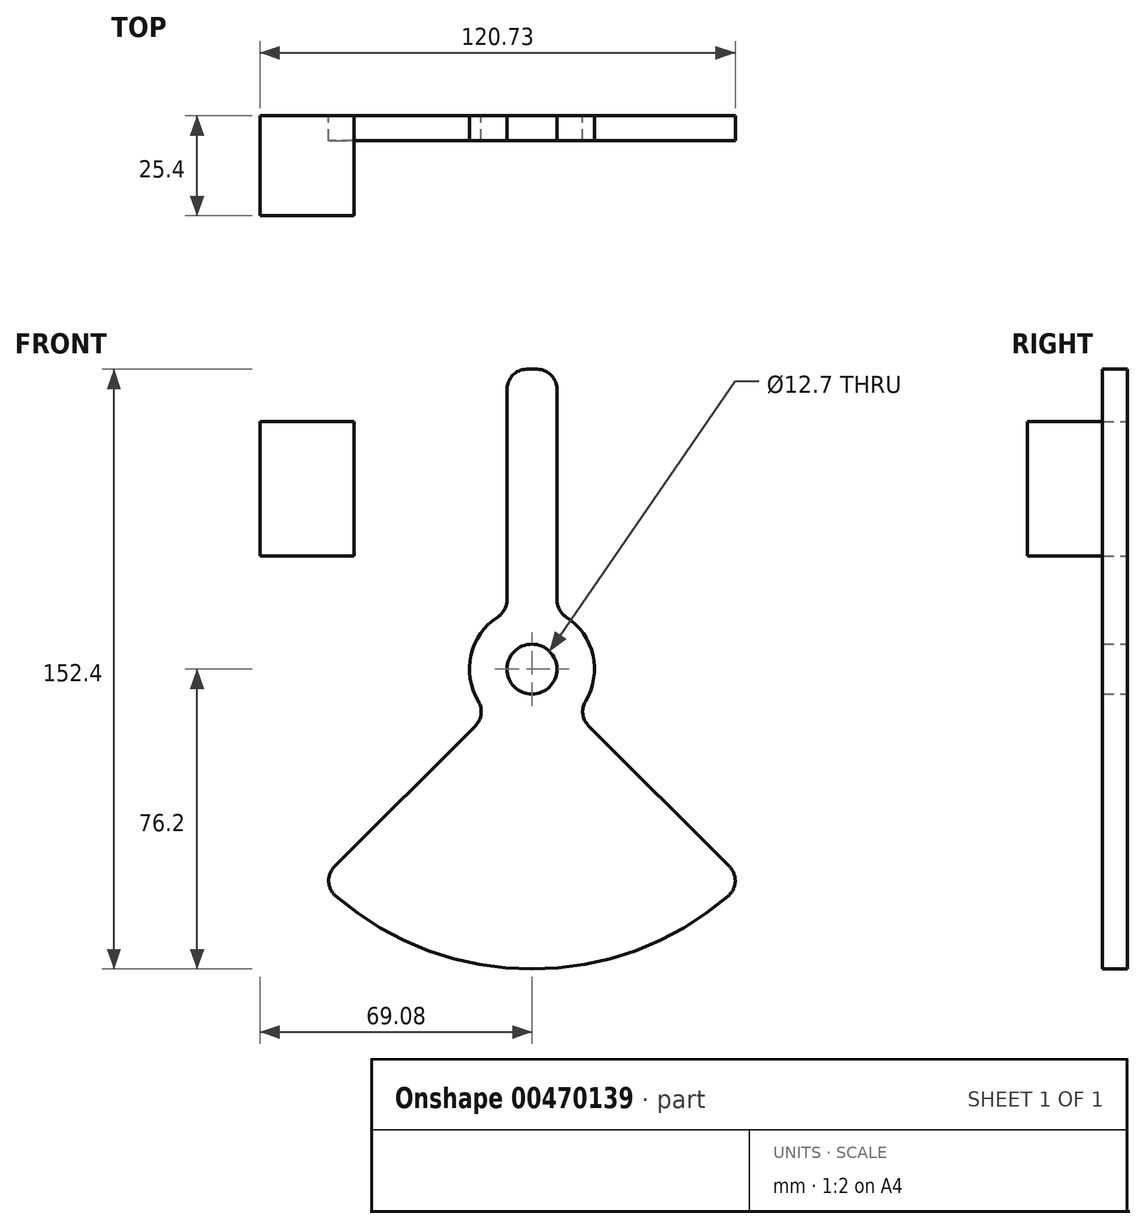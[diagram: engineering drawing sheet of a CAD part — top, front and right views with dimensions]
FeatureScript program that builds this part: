
annotation { "Feature Type Name" : "Feature", "Feature Type Description" : "" }
export const myFeature = defineFeature(function(context is Context, id is Id, definition is map)
    precondition{}
    {
        {
            var Q0;
            Q0=qCreatedBy(makeId("Front.planeOp"),FACE);
            var sketch = newSketch(context, id + "F0", { "sketchPlane" : qUnion([Q0])});
            skCircle(sketch, "E0", {"center": v(0, 0) * mm, "radius": 15.88 * mm});
            skCircle(sketch, "E1", {"center": v(0, 0) * mm, "radius": 76.2 * mm});
            skCircle(sketch, "E2", {"center": v(0, 0) * mm, "radius": 66.67 * mm});
            skCircle(sketch, "E3", {"center": v(0, 0) * mm, "radius": 6.35 * mm});
            skLineSegment(sketch, "E4", {"start": v(-6.35, 14.55) * mm, "end": v(-6.35, 75.93) * mm});
            skLineSegment(sketch, "E5", {"start": v(-6.35, 75.93) * mm, "end": v(6.35, 75.93) * mm, "construction": true});
            skLineSegment(sketch, "E6", {"start": v(6.35, 75.93) * mm, "end": v(6.35, 14.55) * mm});
            skPoint(sketch, "E7", {"position": v(0, 75.93) * mm});
            skLineSegment(sketch, "E8", {"start": v(-11.23, -11.23) * mm, "end": v(-53.88, -53.88) * mm});
            skLineSegment(sketch, "E9", {"start": v(53.88, -53.88) * mm, "end": v(11.23, -11.23) * mm});
            skSolve(sketch);
        }
        {
            var Q0;
            {var subQ0=sQuery(id+"F0.wireOp",EDGE,"E4");var subQ1=sQuery(id+"F0.wireOp",EDGE,"E0");var subQ2=makeQuery(id+"F0.imprint","INTERSECT",VERTEX,{"derivedFrom":[subQ1,subQ0]});Q0=makeQuery(id+"F0.imprint","IMPRINT",FACE,{"disambiguationData":[TD([[makeQuery(id+"F0.imprint","IMPRINT",EDGE,{"disambiguationData":[TD([[subQ2,1.0]])],"derivedFrom":subQ1}),-1.0]])]});}
            var Q1;
            {var subQ0=sQuery(id+"F0.wireOp",EDGE,"E4");var subQ1=sQuery(id+"F0.wireOp",EDGE,"E1");var subQ2=makeQuery(id+"F0.imprint","INTERSECT",VERTEX,{"derivedFrom":[subQ1,subQ0]});Q1=makeQuery(id+"F0.imprint","IMPRINT",FACE,{"disambiguationData":[TD([[makeQuery(id+"F0.imprint","IMPRINT",EDGE,{"disambiguationData":[TD([[subQ2,1.0]])],"derivedFrom":subQ1}),1.0]])]});}
            var Q2;
            Q2=makeQuery(id+"F0.imprint","IMPRINT",FACE,{"disambiguationData":[TD([[makeQuery(id+"F0.imprint","IMPRINT",EDGE,{"derivedFrom":sQuery(id+"F0.wireOp",EDGE,"E3")}),-1.0]])]});
            var Q3;
            {var subQ0=sQuery(id+"F0.wireOp",EDGE,"E8");var subQ1=sQuery(id+"F0.wireOp",EDGE,"E1");var subQ2=makeQuery(id+"F0.imprint","INTERSECT",VERTEX,{"derivedFrom":[subQ1,subQ0]});Q3=makeQuery(id+"F0.imprint","IMPRINT",FACE,{"disambiguationData":[TD([[makeQuery(id+"F0.imprint","IMPRINT",EDGE,{"disambiguationData":[TD([[subQ2,-1.0]])],"derivedFrom":subQ1}),1.0]])]});}
            var Q4;
            {var subQ0=sQuery(id+"F0.wireOp",EDGE,"E8");var subQ1=sQuery(id+"F0.wireOp",EDGE,"E0");var subQ2=makeQuery(id+"F0.imprint","INTERSECT",VERTEX,{"derivedFrom":[subQ1,subQ0]});Q4=makeQuery(id+"F0.imprint","IMPRINT",FACE,{"disambiguationData":[TD([[makeQuery(id+"F0.imprint","IMPRINT",EDGE,{"disambiguationData":[TD([[subQ2,-1.0]])],"derivedFrom":subQ1}),-1.0]])]});}
            extrude(context, id + "F1", {"entities" : qUnion([Q0, Q1, Q2, Q3, Q4]), "depth" : 6.35 * mm});
        }
        {
            var Q0;
            Q0=makeQuery(id+"F1.opExtrude","SWEPT_EDGE",EDGE,{"disambiguationData":[OSD([sQuery(id+"F0.wireOp",EDGE,"E1"),sQuery(id+"F0.wireOp",EDGE,"E6")])]});
            var Q1;
            Q1=makeQuery(id+"F1.opExtrude","SWEPT_EDGE",EDGE,{"disambiguationData":[OSD([sQuery(id+"F0.wireOp",EDGE,"E1"),sQuery(id+"F0.wireOp",EDGE,"E4")])]});
            var Q2;
            Q2=makeQuery(id+"F1.opExtrude","SWEPT_EDGE",EDGE,{"disambiguationData":[OSD([sQuery(id+"F0.wireOp",EDGE,"E0"),sQuery(id+"F0.wireOp",EDGE,"E4")])]});
            var Q3;
            Q3=makeQuery(id+"F1.opExtrude","SWEPT_EDGE",EDGE,{"disambiguationData":[OSD([sQuery(id+"F0.wireOp",EDGE,"E0"),sQuery(id+"F0.wireOp",EDGE,"E8")])]});
            var Q4;
            Q4=makeQuery(id+"F1.opExtrude","SWEPT_EDGE",EDGE,{"disambiguationData":[OSD([sQuery(id+"F0.wireOp",EDGE,"E0"),sQuery(id+"F0.wireOp",EDGE,"E6")])]});
            var Q5;
            Q5=makeQuery(id+"F1.opExtrude","SWEPT_EDGE",EDGE,{"disambiguationData":[OSD([sQuery(id+"F0.wireOp",EDGE,"E0"),sQuery(id+"F0.wireOp",EDGE,"E9")])]});
            var Q6;
            Q6=makeQuery(id+"F1.opExtrude","SWEPT_EDGE",EDGE,{"disambiguationData":[OSD([sQuery(id+"F0.wireOp",EDGE,"E1"),sQuery(id+"F0.wireOp",EDGE,"E9")])]});
            var Q7;
            Q7=makeQuery(id+"F1.opExtrude","SWEPT_EDGE",EDGE,{"disambiguationData":[OSD([sQuery(id+"F0.wireOp",EDGE,"E1"),sQuery(id+"F0.wireOp",EDGE,"E8")])]});
            fillet(context, id + "F2", {"entities" : qUnion([Q0, Q1, Q2, Q3, Q4, Q5, Q6, Q7]), "radius" : 5.08 * mm, "tangentPropagation" : true, "allowEdgeOverflow" : false});
        }
        {
            var Q0;
            Q0=qCreatedBy(makeId("Front.planeOp"),FACE);
            var sketch = newSketch(context, id + "F3", { "sketchPlane" : qUnion([Q0])});
            skLineSegment(sketch, "E10.bottom", {"start": v(-69.08, 62.86) * mm, "end": v(-45.23, 62.86) * mm});
            skLineSegment(sketch, "E10.top", {"start": v(-69.08, 28.8) * mm, "end": v(-45.23, 28.8) * mm});
            skLineSegment(sketch, "E10.left", {"start": v(-69.08, 62.86) * mm, "end": v(-69.08, 28.8) * mm});
            skLineSegment(sketch, "E10.right", {"start": v(-45.23, 62.86) * mm, "end": v(-45.23, 28.8) * mm});
            skSolve(sketch);
        }
        {
            var Q0;
            Q0=makeQuery(id+"F3.imprint","IMPRINT",FACE,{"disambiguationData":[TD([[makeQuery(id+"F3.imprint","IMPRINT",EDGE,{"derivedFrom":sQuery(id+"F3.wireOp",EDGE,"E10.bottom")}),-1.0]])]});
            extrude(context, id + "F4", {"entities" : qUnion([Q0]), "depth" : 25.4 * mm});
        }
    });
